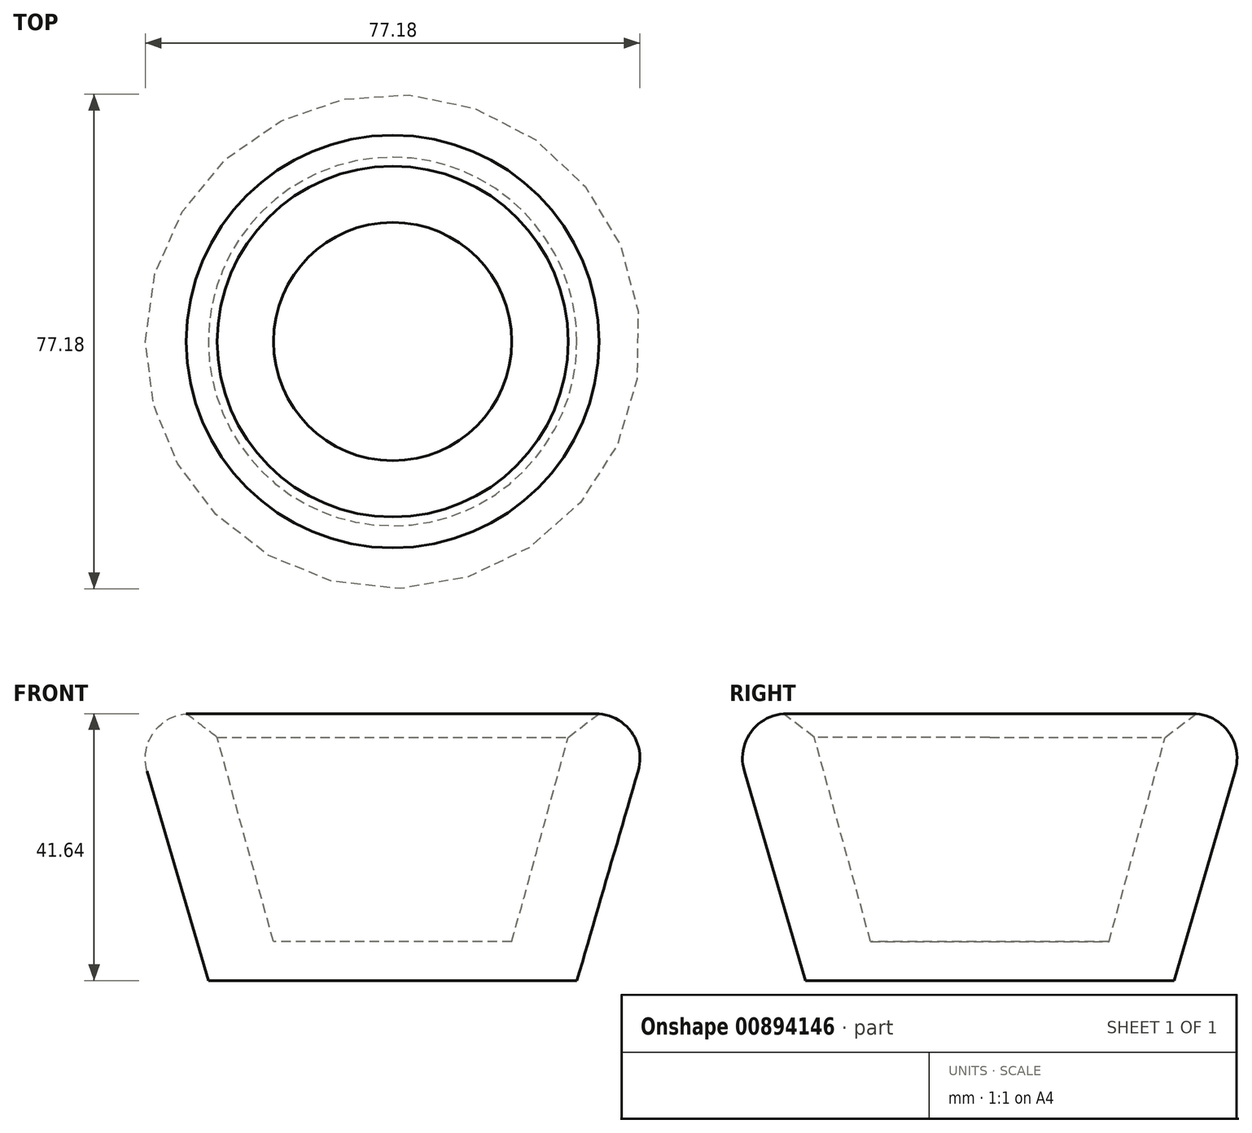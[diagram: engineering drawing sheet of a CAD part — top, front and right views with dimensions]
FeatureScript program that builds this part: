
annotation { "Feature Type Name" : "Feature", "Feature Type Description" : "" }
export const myFeature = defineFeature(function(context is Context, id is Id, definition is map)
    precondition{}
    {
        {
            var Q0;
            Q0=qCreatedBy(makeId("Front.planeOp"),FACE);
            var sketch = newSketch(context, id + "F0", { "sketchPlane" : qUnion([Q0])});
            skLineSegment(sketch, "E0", {"start": v(0, 0) * mm, "end": v(-28.76, 0) * mm});
            skLineSegment(sketch, "E1", {"start": v(-28.76, 0) * mm, "end": v(-40.92, 41.64) * mm});
            skLineSegment(sketch, "E2", {"start": v(-40.92, 41.64) * mm, "end": v(-28.4, 41.64) * mm});
            skLineSegment(sketch, "E3", {"start": v(-28.4, 41.64) * mm, "end": v(-18.6, 6.08) * mm});
            skLineSegment(sketch, "E4", {"start": v(-18.6, 6.08) * mm, "end": v(0, 6.08) * mm});
            skLineSegment(sketch, "E5", {"start": v(0, 6.08) * mm, "end": v(0, 0) * mm});
            skSolve(sketch);
        }
        {
            var Q0;
            Q0=makeQuery(id+"F0.imprint","IMPRINT",FACE,{"disambiguationData":[TD([[makeQuery(id+"F0.imprint","IMPRINT",EDGE,{"derivedFrom":sQuery(id+"F0.wireOp",EDGE,"E0")}),-1.0]])]});
            var Q1;
            Q1=sQuery(id+"F0.wireOp",EDGE,"E5");
            revolve(context, id + "F1", {"surfaceOperationType" : NewSurfaceOperationType.NEW, "entities" : qUnion([Q0]), "axis" : qUnion([Q1]), "revolveType" : RevolveType.FULL});
        }
        {
            var Q0;
            Q0=makeQuery(id+"F1.opRevolve","SWEPT_EDGE",EDGE,{"disambiguationData":[OSD([sQuery(id+"F0.wireOp",EDGE,"E2"),sQuery(id+"F0.wireOp",EDGE,"E3")])]});
            chamfer(context, id + "F2", {"entities" : qUnion([Q0]), "width" : 5 * mm, "tangentPropagation" : true});
        }
        {
            var Q0;
            Q0=makeQuery(id+"F1.opRevolve","SWEPT_EDGE",EDGE,{"disambiguationData":[OSD([sQuery(id+"F0.wireOp",EDGE,"E1"),sQuery(id+"F0.wireOp",EDGE,"E2")])]});
            fillet(context, id + "F3", {"entities" : qUnion([Q0]), "radius" : 7 * mm, "tangentPropagation" : true, "allowEdgeOverflow" : false});
        }
    });
